FCSTD DOCUMENT  (FreeCAD 0.17R10661 (Git))
Label: disc_caliper_mount_jig
License: All rights reserved
LicenseURL: http://en.wikipedia.org/wiki/All_rights_reserved
objects: Sketcher::SketchObject×2
note: 2 computed .brp shape members not serialized (recipe doc carries the construction recipe); baked Part::Feature solids carry a one-line shape summary decoded from their .brp

FEATURE [Sketcher::SketchObject] Sketch
  sketch-geometry (32):
    g0: LineSegment [constr] StartX=14.1 StartY=130 StartZ=0 EndX=45.9 EndY=130 EndZ=0
    g1: LineSegment [constr] StartX=45.9 StartY=130 StartZ=0 EndX=45.9 EndY=30 EndZ=0
    g2: LineSegment [constr] StartX=45.9 StartY=30 StartZ=0 EndX=14.1 EndY=30 EndZ=0
    g3: LineSegment [constr] StartX=14.1 StartY=30 StartZ=0 EndX=14.1 EndY=130 EndZ=0
    g4: LineSegment [constr] StartX=30 StartY=130 StartZ=0 EndX=30 EndY=0 EndZ=0
    g5: Circle CenterX=54.38 CenterY=68.2877 CenterZ=0 NormalX=0 NormalY=0 NormalZ=1 Radius=2.5
    g6: Circle CenterX=46.3558 CenterY=17.9229 CenterZ=0 NormalX=0 NormalY=0 NormalZ=1 Radius=2.5
    g7: LineSegment [constr] StartX=0 StartY=0 StartZ=0 EndX=54.38 EndY=68.2877 EndZ=0
    g8: LineSegment [constr] StartX=0 StartY=0 StartZ=0 EndX=46.3558 EndY=17.9229 EndZ=0
    g9: LineSegment StartX=-10 StartY=10 StartZ=0 EndX=40.8558 EndY=10 EndZ=0
    g10: LineSegment StartX=40.8558 StartY=10 StartZ=0 EndX=40.8558 EndY=23.4229 EndZ=0
    g11: LineSegment StartX=40.8558 StartY=23.4229 StartZ=0 EndX=57.9 EndY=23.4229 EndZ=0
    g12: LineSegment StartX=57.9 StartY=23.4229 StartZ=0 EndX=57.9 EndY=62.7877 EndZ=0
    g13: LineSegment StartX=57.9 StartY=62.7877 StartZ=0 EndX=48.88 EndY=62.7877 EndZ=0
    g14: LineSegment StartX=48.88 StartY=62.7877 StartZ=0 EndX=48.88 EndY=73.7877 EndZ=0
    g15: LineSegment StartX=48.88 StartY=73.7877 StartZ=0 EndX=82.9 EndY=73.7877 EndZ=0
    g16: LineSegment StartX=82.9 StartY=73.7877 StartZ=0 EndX=82.9 EndY=-15 EndZ=0
    g17: LineSegment StartX=82.9 StartY=-15 StartZ=0 EndX=-10 EndY=-15 EndZ=0
    g18: LineSegment StartX=-10 StartY=-15 StartZ=0 EndX=-10 EndY=10 EndZ=0
    g19: LineSegment [constr] StartX=48.88 StartY=68.2877 StartZ=0 EndX=51.88 EndY=68.2877 EndZ=0
    g20: LineSegment [constr] StartX=54.38 StartY=65.7877 StartZ=0 EndX=54.38 EndY=62.7877 EndZ=0
    g21: LineSegment [constr] StartX=54.38 StartY=70.7877 StartZ=0 EndX=54.38 EndY=73.7877 EndZ=0
    g22: LineSegment [constr] StartX=46.3558 StartY=20.4229 StartZ=0 EndX=46.3558 EndY=23.4229 EndZ=0
    g23: LineSegment [constr] StartX=43.8558 StartY=17.9229 StartZ=0 EndX=40.8558 EndY=17.9229 EndZ=0
    g24: LineSegment [constr] StartX=0 StartY=0 StartZ=0 EndX=0 EndY=10 EndZ=0
    g25: LineSegment [constr] StartX=0 StartY=0 StartZ=0 EndX=-10 EndY=0 EndZ=0
    g26: LineSegment [constr] StartX=0 StartY=0 StartZ=0 EndX=0 EndY=-15 EndZ=0
    g27: Circle CenterX=0 CenterY=0 CenterZ=0 NormalX=0 NormalY=0 NormalZ=1 Radius=4.5
    g28: LineSegment [constr] StartX=61.6248 StartY=89.3246 StartZ=0 EndX=112.536 EndY=38.4129 EndZ=0
    g29: LineSegment [constr] StartX=112.536 StartY=38.4129 StartZ=0 EndX=29.0979 EndY=-45.0257 EndZ=0
    g30: LineSegment [constr] StartX=29.0979 StartY=-45.0257 StartZ=0 EndX=-21.8138 EndY=5.88597 EndZ=0
    g31: LineSegment [constr] StartX=-21.8138 StartY=5.88597 StartZ=0 EndX=61.6248 EndY=89.3246 EndZ=0
  constraints (102):
    c: Coincident(g0,g1)
    c: Coincident(g1,g2)
    c: Coincident(g2,g3)
    c: Coincident(g3,g0)
    c: Horizontal(g0)
    c: Horizontal(g2)
    c: Vertical(g1)
    c: Vertical(g3)
    c: Vertical(g4)
    c: PointOnObject(g4,g-1)
    c: Symmetric(g0,g0,g4)
    c: Distance(g0) = 31.8
    c: Distance(g-1,g4) = 30
    c: DistanceY(g-1,g2) = 30
    c: Radius(g5) = 2.5
    c: Radius(g6) = 2.5
    c: Distance(g6,g5) = 51
    c: Coincident(g7,g-1)
    c: Coincident(g7,g5)
    c: Coincident(g8,g-1)
    c: Angle(g8,g7) = 0.529358
    c: Coincident(g8,g6)
    c: Distance(g8) = 49.7
    c: Coincident(g10,g11)
    c: Coincident(g11,g12)
    c: Coincident(g12,g13)
    c: Coincident(g13,g14)
    c: Coincident(g14,g15)
    c: Coincident(g18,g9)
    c: Parallel(g9,g17)
    c: Perpendicular(g10,g11)
    c: Perpendicular(g14,g13)
    c: Perpendicular(g15,g14)
    c: Parallel(g12,g16)
    c: Coincident(g9,g10)
    c: PointOnObject(g19,g14)
    c: PointOnObject(g19,g5)
    c: Perpendicular(g5,g19)
    c: Perpendicular(g14,g19)
    c: Distance(g19) = 3
    c: PointOnObject(g20,g5)
    c: PointOnObject(g20,g13)
    c: Perpendicular(g13,g20)
    c: Perpendicular(g5,g20)
    c: Distance(g20) = 3
    c: PointOnObject(g21,g5)
    c: PointOnObject(g21,g15)
    c: Perpendicular(g15,g21)
    c: Perpendicular(g5,g21)
    c: Distance(g21) = 3
    c: PointOnObject(g22,g6)
    c: PointOnObject(g22,g11)
    c: Perpendicular(g6,g22)
    c: Perpendicular(g11,g22)
    c: Distance(g22) = 3
    c: PointOnObject(g23,g6)
    c: PointOnObject(g23,g10)
    c: Perpendicular(g10,g23)
    c: Perpendicular(g6,g23)
    c: Distance(g23) = 3
    c: Coincident(g24,g-1)
    c: PointOnObject(g24,g9)
    c: Perpendicular(g9,g24)
    c: Distance(g24) = 10
    c: Coincident(g25,g-1)
    c: PointOnObject(g25,g18)
    c: Perpendicular(g18,g25)
    c: Distance(g25) = 10
    c: Coincident(g26,g-1)
    c: PointOnObject(g26,g17)
    c: Perpendicular(g17,g26)
    c: Coincident(g27,g-1)
    c: Radius(g27) = 4.5
    c: Vertical(g12)
    c: Perpendicular(g12,g11)
    c: Horizontal(g15)
    c: Distance(g1,g12) = 12
    c: Vertical(g18)
    c: Horizontal(g9)
    c: Coincident(g28,g29)
    c: Coincident(g29,g30)
    c: Coincident(g30,g31)
    c: Coincident(g31,g28)
    c: Perpendicular(g28,g31)
    c: Perpendicular(g31,g30)
    c: Perpendicular(g29,g30)
    c: Distance(g30) = 72
    c: Distance(g29) = 118
    c: Distance(g6,g31) = 39.6918
    c: Distance(g6,g30) = 56.7146
    c: Distance(g5,g31) = 9.75246
    c: Distance(g3) = 100
    c: DistanceX(g30) = -21.8138
    c: DistanceY(g30) = 5.88597
    c: Angle(g30) = 2.35619
    c: DistanceX(g5) = 54.38
    c: Coincident(g15,g16)
    c: Coincident(g16,g17)
    c: Distance(g11,g16) = 25
    c: Coincident(g18,g17)
    c: Distance(g9,g17) = 25
    c: PointOnObject(g4,g0)
FEATURE [Sketcher::SketchObject] Sketch001
  sketch-geometry (30):
    g0: LineSegment [constr] StartX=14.1 StartY=130 StartZ=0 EndX=45.9 EndY=130 EndZ=0
    g1: LineSegment [constr] StartX=45.9 StartY=130 StartZ=0 EndX=45.9 EndY=30 EndZ=0
    g2: LineSegment [constr] StartX=45.9 StartY=30 StartZ=0 EndX=14.1 EndY=30 EndZ=0
    g3: LineSegment [constr] StartX=14.1 StartY=30 StartZ=0 EndX=14.1 EndY=130 EndZ=0
    g4: LineSegment [constr] StartX=30 StartY=130 StartZ=0 EndX=30 EndY=0 EndZ=0
    g5: Circle CenterX=54.38 CenterY=68.2877 CenterZ=0 NormalX=0 NormalY=0 NormalZ=1 Radius=2.5
    g6: Circle CenterX=46.3558 CenterY=17.9229 CenterZ=0 NormalX=0 NormalY=0 NormalZ=1 Radius=2.5
    g7: LineSegment [constr] StartX=0 StartY=0 StartZ=0 EndX=54.38 EndY=68.2877 EndZ=0
    g8: LineSegment [constr] StartX=0 StartY=0 StartZ=0 EndX=46.3558 EndY=17.9229 EndZ=0
    g9: LineSegment StartX=48.88 StartY=73.7877 StartZ=0 EndX=82.9 EndY=73.7877 EndZ=0
    g10: LineSegment StartX=82.9 StartY=73.7877 StartZ=0 EndX=82.9 EndY=-15 EndZ=0
    g11: LineSegment StartX=82.9 StartY=-15 StartZ=0 EndX=-10 EndY=-15 EndZ=0
    g12: LineSegment StartX=-10 StartY=-15 StartZ=0 EndX=-10 EndY=10 EndZ=0
    g13: LineSegment [constr] StartX=48.88 StartY=68.2877 StartZ=0 EndX=51.88 EndY=68.2877 EndZ=0
    g14: LineSegment [constr] StartX=54.38 StartY=65.7877 StartZ=0 EndX=54.38 EndY=62.7877 EndZ=0
    g15: LineSegment [constr] StartX=54.38 StartY=70.7877 StartZ=0 EndX=54.38 EndY=73.7877 EndZ=0
    g16: LineSegment [constr] StartX=46.3558 StartY=20.4229 StartZ=0 EndX=46.3558 EndY=23.4229 EndZ=0
    g17: LineSegment [constr] StartX=43.8558 StartY=17.9229 StartZ=0 EndX=40.8558 EndY=17.9229 EndZ=0
    g18: LineSegment [constr] StartX=0 StartY=0 StartZ=0 EndX=0 EndY=10 EndZ=0
    g19: LineSegment [constr] StartX=0 StartY=0 StartZ=0 EndX=-10 EndY=0 EndZ=0
    g20: LineSegment [constr] StartX=0 StartY=0 StartZ=0 EndX=0 EndY=-15 EndZ=0
    g21: Circle CenterX=0 CenterY=0 CenterZ=0 NormalX=0 NormalY=0 NormalZ=1 Radius=4.5
    g22: LineSegment [constr] StartX=61.6248 StartY=89.3246 StartZ=0 EndX=112.536 EndY=38.4129 EndZ=0
    g23: LineSegment [constr] StartX=112.536 StartY=38.4129 StartZ=0 EndX=29.0979 EndY=-45.0257 EndZ=0
    g24: LineSegment [constr] StartX=29.0979 StartY=-45.0257 StartZ=0 EndX=-21.8138 EndY=5.88597 EndZ=0
    g25: LineSegment [constr] StartX=-21.8138 StartY=5.88597 StartZ=0 EndX=61.6248 EndY=89.3246 EndZ=0
    g26: LineSegment StartX=-10 StartY=10 StartZ=0 EndX=40.8558 EndY=10 EndZ=0
    g27: LineSegment StartX=40.8558 StartY=10 StartZ=0 EndX=40.8558 EndY=23.4229 EndZ=0
    g28: LineSegment StartX=40.8558 StartY=23.4229 StartZ=0 EndX=48.88 EndY=23.4229 EndZ=0
    g29: LineSegment StartX=48.88 StartY=23.4229 StartZ=0 EndX=48.88 EndY=73.7877 EndZ=0
  constraints (88):
    c: Coincident(g0,g1)
    c: Coincident(g1,g2)
    c: Coincident(g2,g3)
    c: Coincident(g3,g0)
    c: Horizontal(g0)
    c: Horizontal(g2)
    c: Vertical(g1)
    c: Vertical(g3)
    c: Vertical(g4)
    c: PointOnObject(g4,g-1)
    c: Symmetric(g0,g0,g4)
    c: Distance(g0) = 31.8
    c: Distance(g-1,g4) = 30
    c: DistanceY(g-1,g2) = 30
    c: Radius(g5) = 2.5
    c: Radius(g6) = 2.5
    c: Distance(g6,g5) = 51
    c: Coincident(g7,g-1)
    c: Coincident(g7,g5)
    c: Coincident(g8,g-1)
    c: Angle(g8,g7) = 0.529358
    c: Coincident(g8,g6)
    c: Distance(g8) = 49.7
    c: PointOnObject(g13,g5)
    c: Perpendicular(g5,g13)
    c: Distance(g13) = 3
    c: PointOnObject(g14,g5)
    c: Perpendicular(g5,g14)
    c: Distance(g14) = 3
    c: PointOnObject(g15,g5)
    c: PointOnObject(g15,g9)
    c: Perpendicular(g9,g15)
    c: Perpendicular(g5,g15)
    c: Distance(g15) = 3
    c: PointOnObject(g16,g6)
    c: Perpendicular(g6,g16)
    c: Distance(g16) = 3
    c: PointOnObject(g17,g6)
    c: Perpendicular(g6,g17)
    c: Distance(g17) = 3
    c: Coincident(g18,g-1)
    c: Distance(g18) = 10
    c: Coincident(g19,g-1)
    c: PointOnObject(g19,g12)
    c: Perpendicular(g12,g19)
    c: Distance(g19) = 10
    c: Coincident(g20,g-1)
    c: PointOnObject(g20,g11)
    c: Perpendicular(g11,g20)
    c: Coincident(g21,g-1)
    c: Radius(g21) = 4.5
    c: Horizontal(g9)
    c: Vertical(g12)
    c: Coincident(g22,g23)
    c: Coincident(g23,g24)
    c: Coincident(g24,g25)
    c: Coincident(g25,g22)
    c: Perpendicular(g22,g25)
    c: Perpendicular(g25,g24)
    c: Perpendicular(g23,g24)
    c: Distance(g24) = 72
    c: Distance(g23) = 118
    c: Distance(g6,g25) = 39.6918
    c: Distance(g6,g24) = 56.7146
    c: Distance(g5,g25) = 9.75246
    c: Distance(g3) = 100
    c: DistanceX(g24) = -21.8138
    c: DistanceY(g24) = 5.88597
    c: Angle(g24) = 2.35619
    c: DistanceX(g5) = 54.38
    c: Coincident(g9,g10)
    c: Coincident(g10,g11)
    c: Coincident(g12,g11)
    c: PointOnObject(g4,g0)
    c: Coincident(g12,g26)
    c: Horizontal(g26)
    c: PointOnObject(g18,g26)
    c: Vertical(g18)
    c: Coincident(g27,g26)
    c: Vertical(g27)
    c: Coincident(g28,g27)
    c: Horizontal(g28)
    c: Coincident(g29,g28)
    c: Vertical(g29)
    c: Coincident(g29,g9)
    c: PointOnObject(g13,g29)
    c: PointOnObject(g16,g28)
    c: PointOnObject(g17,g27)
